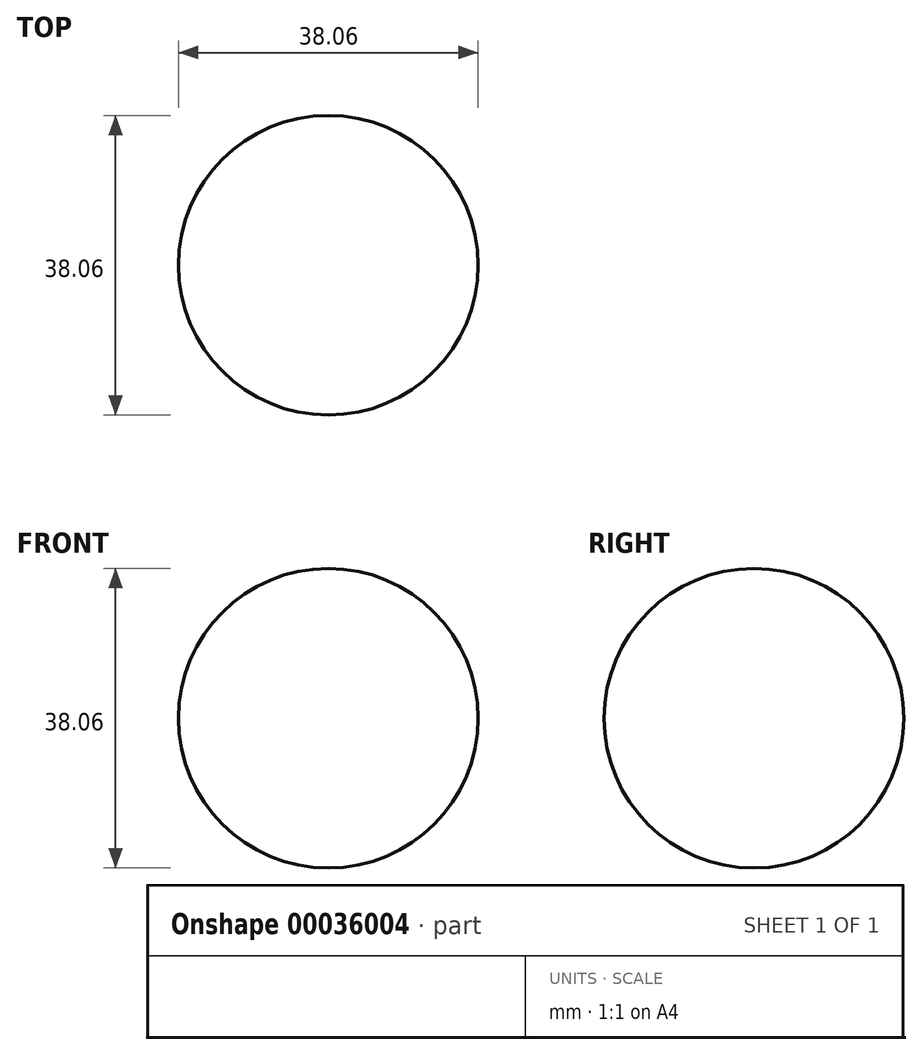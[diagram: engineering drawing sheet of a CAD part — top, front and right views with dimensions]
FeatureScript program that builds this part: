
annotation { "Feature Type Name" : "Feature", "Feature Type Description" : "" }
export const myFeature = defineFeature(function(context is Context, id is Id, definition is map)
    precondition{}
    {
        {
            var Q0;
            Q0=qCreatedBy(makeId("Front.planeOp"),FACE);
            var sketch = newSketch(context, id + "F0", { "sketchPlane" : qUnion([Q0])});
            skArc(sketch, "E0", {"start": v(0, -19.03) * mm, "mid": v(19.03, 0) * mm, "end": v(0, 19.03) * mm});
            skLineSegment(sketch, "E1", {"start": v(0, 19.03) * mm, "end": v(0, -19.03) * mm});
            skSolve(sketch);
        }
        {
            var Q0;
            Q0=makeQuery(id+"F0.imprint","IMPRINT",FACE,{"disambiguationData":[TD([[makeQuery(id+"F0.imprint","IMPRINT",EDGE,{"derivedFrom":sQuery(id+"F0.wireOp",EDGE,"E0")}),1.0]])]});
            var Q1;
            Q1=sQuery(id+"F0.wireOp",EDGE,"E1");
            revolve(context, id + "F1", {"entities" : qUnion([Q0]), "axis" : qUnion([Q1]), "revolveType" : RevolveType.FULL});
        }
    });
